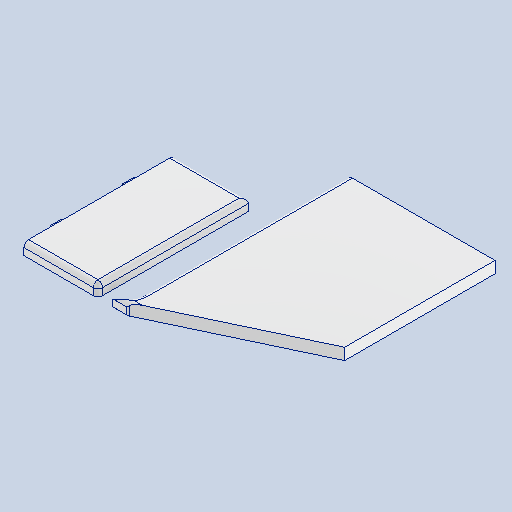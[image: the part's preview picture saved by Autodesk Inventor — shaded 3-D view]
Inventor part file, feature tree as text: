
AUTODESK INVENTOR PART (.ipt)
format: ipt  version: 2025 (Build 290162010, 162A)  size: 183,296 bytes
history: native  units: mm
features: reference x10, sketch x5, other x4, extrude x3, sweep x1, fillet x1
ambient origin geometry x8: Origin, YZ Plane, XZ Plane, XY Plane, X Axis, Y Axis, Z Axis, Center Point
bodies: Volumenkörper1 (feature_tree)
feature tree (24):
  extrude  "Extrusion1"  Depth=2.5mm
  extrude  "Extrusion3"  Depth=2.5mm
  sweep  "Sweeping2"
  fillet  "Rundung3"  Radius=10.0mm
  extrude  "Extrusion4"  Depth=2.0mm
  sketch  "Skizze1"  dims[d0=5.0mm d1=0.0mm d7=2.5mm]
  reference  "Referenz35"
  reference  "Referenz37"
  sketch  "Skizze5"  dims[d8=5.0mm d9=2.5mm]
  reference  "Referenz54"
  reference  "Referenz55"
  reference  "Referenz56"
  reference  "Referenz57"
  reference  "Referenz58"
  reference  "Referenz59"
  sketch  "Skizze6"  dims[d10=5.0mm d11=3.0mm d12=0.0mm d14=10.0mm]
  sketch  "Skizze7"  dims[d15=0.0mm d16=0.0mm d17=2.0mm]
  sketch  "Skizze8"  dims[d18=3.3mm d19=0.0mm d4=0.0mm d5=0.0mm d6=0.0mm]
  reference  "Referenz61"
  reference  "Referenz62"
  other  "<userpath>\GIT\HDVKBM\CAD\Krandemonstrator\Schlitten.iam"
  other  "Schlitten.iam"
  other  "SchlittenS:1"
  other  "SchlittenDeckel:1"
